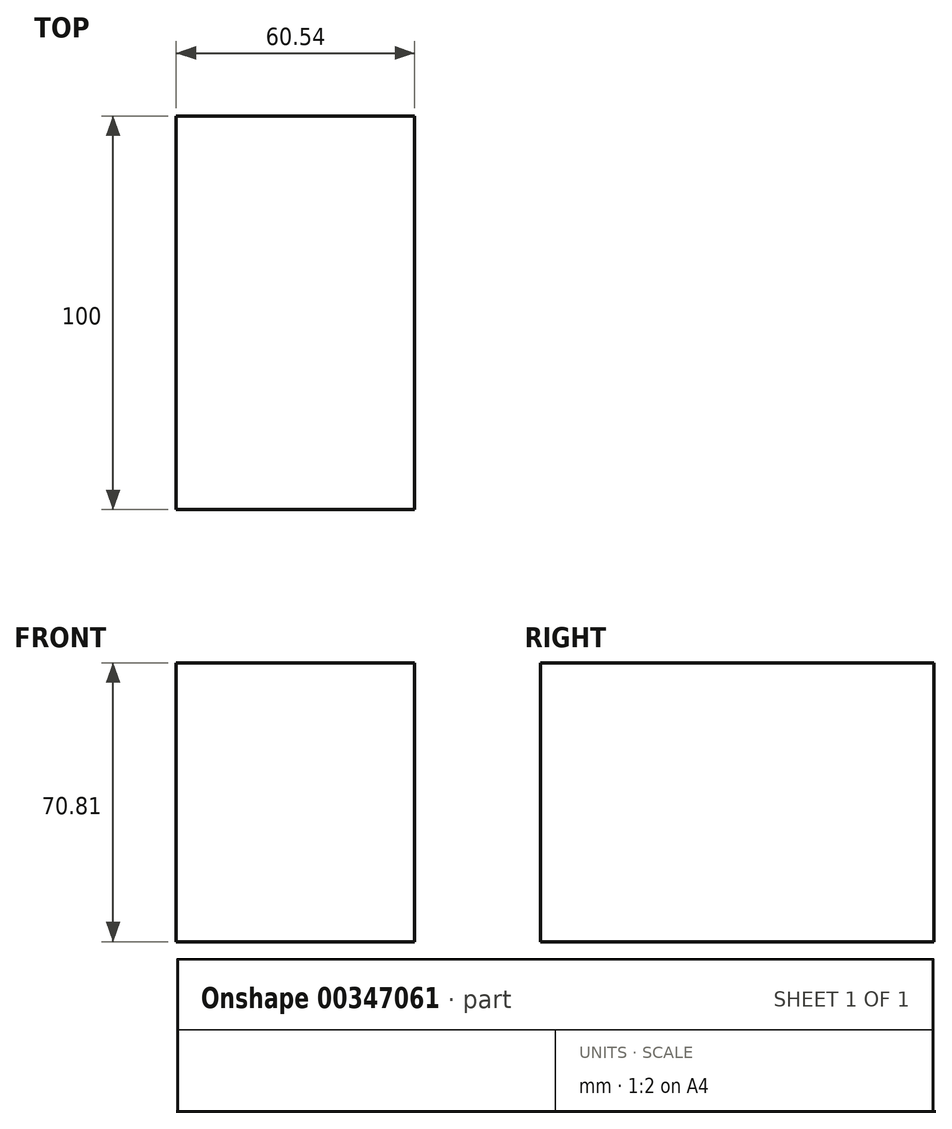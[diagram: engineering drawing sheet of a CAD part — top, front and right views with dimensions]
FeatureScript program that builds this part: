
annotation { "Feature Type Name" : "Feature", "Feature Type Description" : "" }
export const myFeature = defineFeature(function(context is Context, id is Id, definition is map)
    precondition{}
    {
        {
            var Q0;
            Q0=qCreatedBy(makeId("Front.planeOp"),FACE);
            var sketch = newSketch(context, id + "F0", { "sketchPlane" : qUnion([Q0])});
            skLineSegment(sketch, "E0.bottom", {"start": v(0, 0) * mm, "end": v(0, 0) * mm});
            skLineSegment(sketch, "E0.top", {"start": v(0, 0) * mm, "end": v(0, 0) * mm});
            skLineSegment(sketch, "E0.left", {"start": v(0, 0) * mm, "end": v(0, 0) * mm});
            skLineSegment(sketch, "E0.right", {"start": v(0, 0) * mm, "end": v(0, 0) * mm});
            skLineSegment(sketch, "E1.bottom", {"start": v(0, 0) * mm, "end": v(60.54, 0) * mm});
            skLineSegment(sketch, "E1.top", {"start": v(0, 70.81) * mm, "end": v(60.54, 70.81) * mm});
            skLineSegment(sketch, "E1.left", {"start": v(0, 0) * mm, "end": v(0, 70.81) * mm});
            skLineSegment(sketch, "E1.right", {"start": v(60.54, 0) * mm, "end": v(60.54, 70.81) * mm});
            skSolve(sketch);
        }
        {
            var Q0;
            Q0=makeQuery(id+"F0.imprint","IMPRINT",FACE,{"disambiguationData":[TD([[makeQuery(id+"F0.imprint","IMPRINT",EDGE,{"derivedFrom":sQuery(id+"F0.wireOp",EDGE,"E1.bottom")}),1.0]])]});
            extrude(context, id + "F1", {"entities" : qUnion([Q0]), "depth" : 100 * mm});
        }
    });
